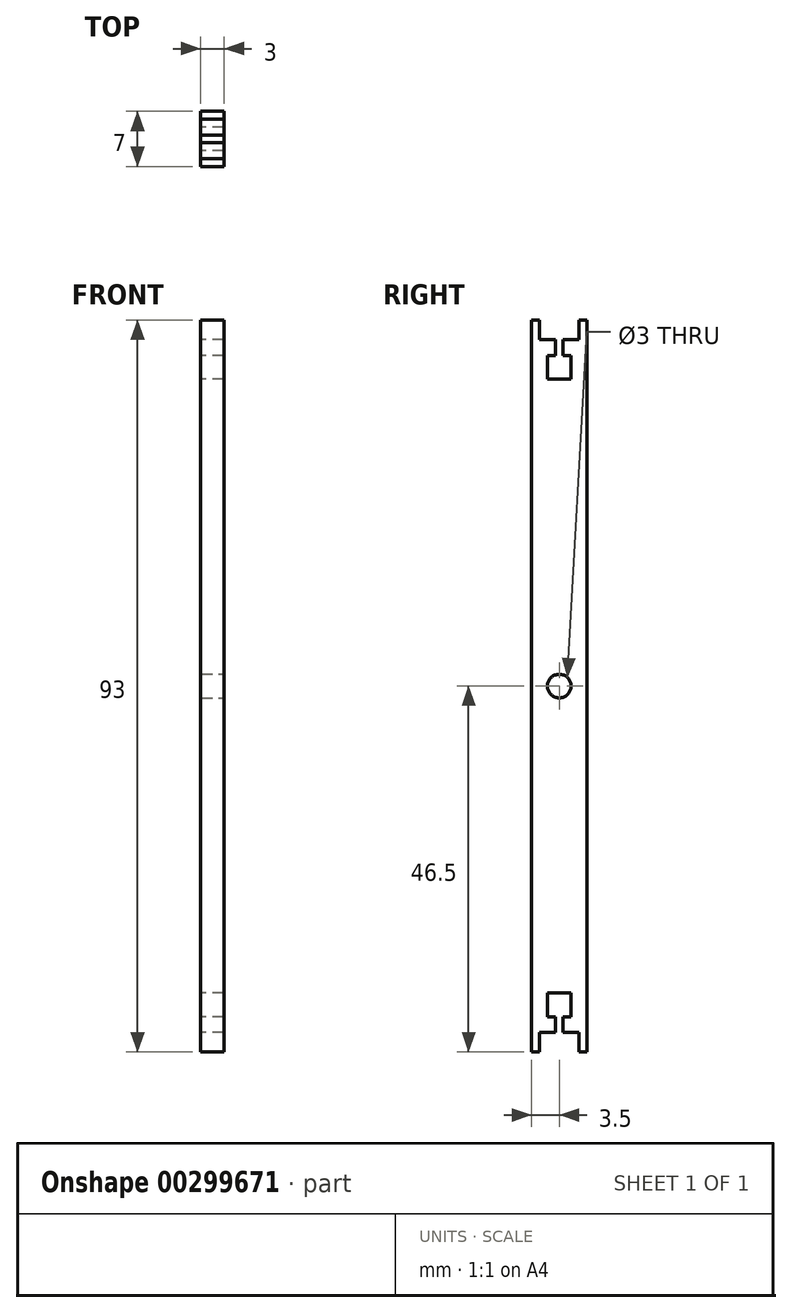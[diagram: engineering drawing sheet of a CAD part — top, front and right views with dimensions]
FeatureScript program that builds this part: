
annotation { "Feature Type Name" : "Feature", "Feature Type Description" : "" }
export const myFeature = defineFeature(function(context is Context, id is Id, definition is map)
    precondition{}
    {
        {
            var Q0;
            Q0=qCreatedBy(makeId("Right.planeOp"),FACE);
            var sketch = newSketch(context, id + "F0", { "sketchPlane" : qUnion([Q0])});
            skLineSegment(sketch, "E0", {"start": v(0, 0) * mm, "end": v(0, 93) * mm});
            skLineSegment(sketch, "E1", {"start": v(0, 93) * mm, "end": v(1, 93) * mm});
            skLineSegment(sketch, "E2", {"start": v(1, 93) * mm, "end": v(1, 90.5) * mm});
            skLineSegment(sketch, "E3", {"start": v(1, 90.5) * mm, "end": v(3, 90.5) * mm});
            skLineSegment(sketch, "E4", {"start": v(3, 90.5) * mm, "end": v(3, 88.5) * mm});
            skLineSegment(sketch, "E5", {"start": v(3, 88.5) * mm, "end": v(2, 88.5) * mm});
            skLineSegment(sketch, "E6", {"start": v(2, 88.5) * mm, "end": v(2, 85.5) * mm});
            skLineSegment(sketch, "E7", {"start": v(2, 85.5) * mm, "end": v(5, 85.5) * mm});
            skLineSegment(sketch, "E8", {"start": v(5, 85.5) * mm, "end": v(5, 88.5) * mm});
            skLineSegment(sketch, "E9", {"start": v(5, 88.5) * mm, "end": v(4, 88.5) * mm});
            skLineSegment(sketch, "E10", {"start": v(4, 88.5) * mm, "end": v(4, 90.5) * mm});
            skLineSegment(sketch, "E11", {"start": v(4, 90.5) * mm, "end": v(6, 90.5) * mm});
            skLineSegment(sketch, "E12", {"start": v(6, 90.5) * mm, "end": v(6, 93) * mm});
            skLineSegment(sketch, "E13", {"start": v(6, 93) * mm, "end": v(7, 93) * mm});
            skLineSegment(sketch, "E14", {"start": v(7, 93) * mm, "end": v(7, 0) * mm});
            skLineSegment(sketch, "E15", {"start": v(7, 0) * mm, "end": v(6, 0) * mm});
            skLineSegment(sketch, "E16", {"start": v(6, 0) * mm, "end": v(6, 2.5) * mm});
            skLineSegment(sketch, "E17", {"start": v(6, 2.5) * mm, "end": v(4, 2.5) * mm});
            skLineSegment(sketch, "E18", {"start": v(4, 2.5) * mm, "end": v(4, 4.5) * mm});
            skLineSegment(sketch, "E19", {"start": v(4, 4.5) * mm, "end": v(5, 4.5) * mm});
            skLineSegment(sketch, "E20", {"start": v(5, 4.5) * mm, "end": v(5, 7.5) * mm});
            skLineSegment(sketch, "E21", {"start": v(5, 7.5) * mm, "end": v(2, 7.5) * mm});
            skLineSegment(sketch, "E22", {"start": v(2, 7.5) * mm, "end": v(2, 4.5) * mm});
            skLineSegment(sketch, "E23", {"start": v(2, 4.5) * mm, "end": v(3, 4.5) * mm});
            skLineSegment(sketch, "E24", {"start": v(3, 4.5) * mm, "end": v(3, 2.5) * mm});
            skLineSegment(sketch, "E25", {"start": v(3, 2.5) * mm, "end": v(1, 2.5) * mm});
            skLineSegment(sketch, "E26", {"start": v(1, 2.5) * mm, "end": v(1, 0) * mm});
            skLineSegment(sketch, "E27", {"start": v(1, 0) * mm, "end": v(0, 0) * mm});
            skSolve(sketch);
        }
        {
            var Q0;
            Q0 = qSketchRegion(id + "F0", true);
            extrude(context, id + "F1", {"entities" : qUnion([Q0]), "depth" : 3 * mm});
        }
        {
            var Q0;
            Q0=makeQuery(id+"F1.opExtrude","CAP_FACE",FACE,{"disambiguationData":[OSD([sQuery(id+"F0.wireOp",EDGE,"E0"),sQuery(id+"F0.wireOp",EDGE,"E1"),sQuery(id+"F0.wireOp",EDGE,"E2"),sQuery(id+"F0.wireOp",EDGE,"E3"),sQuery(id+"F0.wireOp",EDGE,"E4"),sQuery(id+"F0.wireOp",EDGE,"E5"),sQuery(id+"F0.wireOp",EDGE,"E6"),sQuery(id+"F0.wireOp",EDGE,"E7"),sQuery(id+"F0.wireOp",EDGE,"E8"),sQuery(id+"F0.wireOp",EDGE,"E9"),sQuery(id+"F0.wireOp",EDGE,"E10"),sQuery(id+"F0.wireOp",EDGE,"E11"),sQuery(id+"F0.wireOp",EDGE,"E12"),sQuery(id+"F0.wireOp",EDGE,"E13"),sQuery(id+"F0.wireOp",EDGE,"E14"),sQuery(id+"F0.wireOp",EDGE,"E15"),sQuery(id+"F0.wireOp",EDGE,"E16"),sQuery(id+"F0.wireOp",EDGE,"E17"),sQuery(id+"F0.wireOp",EDGE,"E18"),sQuery(id+"F0.wireOp",EDGE,"E19"),sQuery(id+"F0.wireOp",EDGE,"E20"),sQuery(id+"F0.wireOp",EDGE,"E21"),sQuery(id+"F0.wireOp",EDGE,"E22"),sQuery(id+"F0.wireOp",EDGE,"E23"),sQuery(id+"F0.wireOp",EDGE,"E24"),sQuery(id+"F0.wireOp",EDGE,"E25"),sQuery(id+"F0.wireOp",EDGE,"E26"),sQuery(id+"F0.wireOp",EDGE,"E27")])],"isStart":false});
            var sketch = newSketch(context, id + "F2", { "sketchPlane" : qUnion([Q0])});
            skCircle(sketch, "E28", {"center": v(3.5, 46.5) * mm, "radius": 1.5 * mm});
            skSolve(sketch);
        }
        {
            var Q0;
            Q0 = qSketchRegion(id + "F2", true);
            extrude(context, id + "F3", {"entities" : qUnion([Q0]), "operationType" : NewBodyOperationType.REMOVE, "endBound" : BoundingType.THROUGH_ALL, "oppositeDirection" : true, "depth" : 25 * mm});
        }
    });
